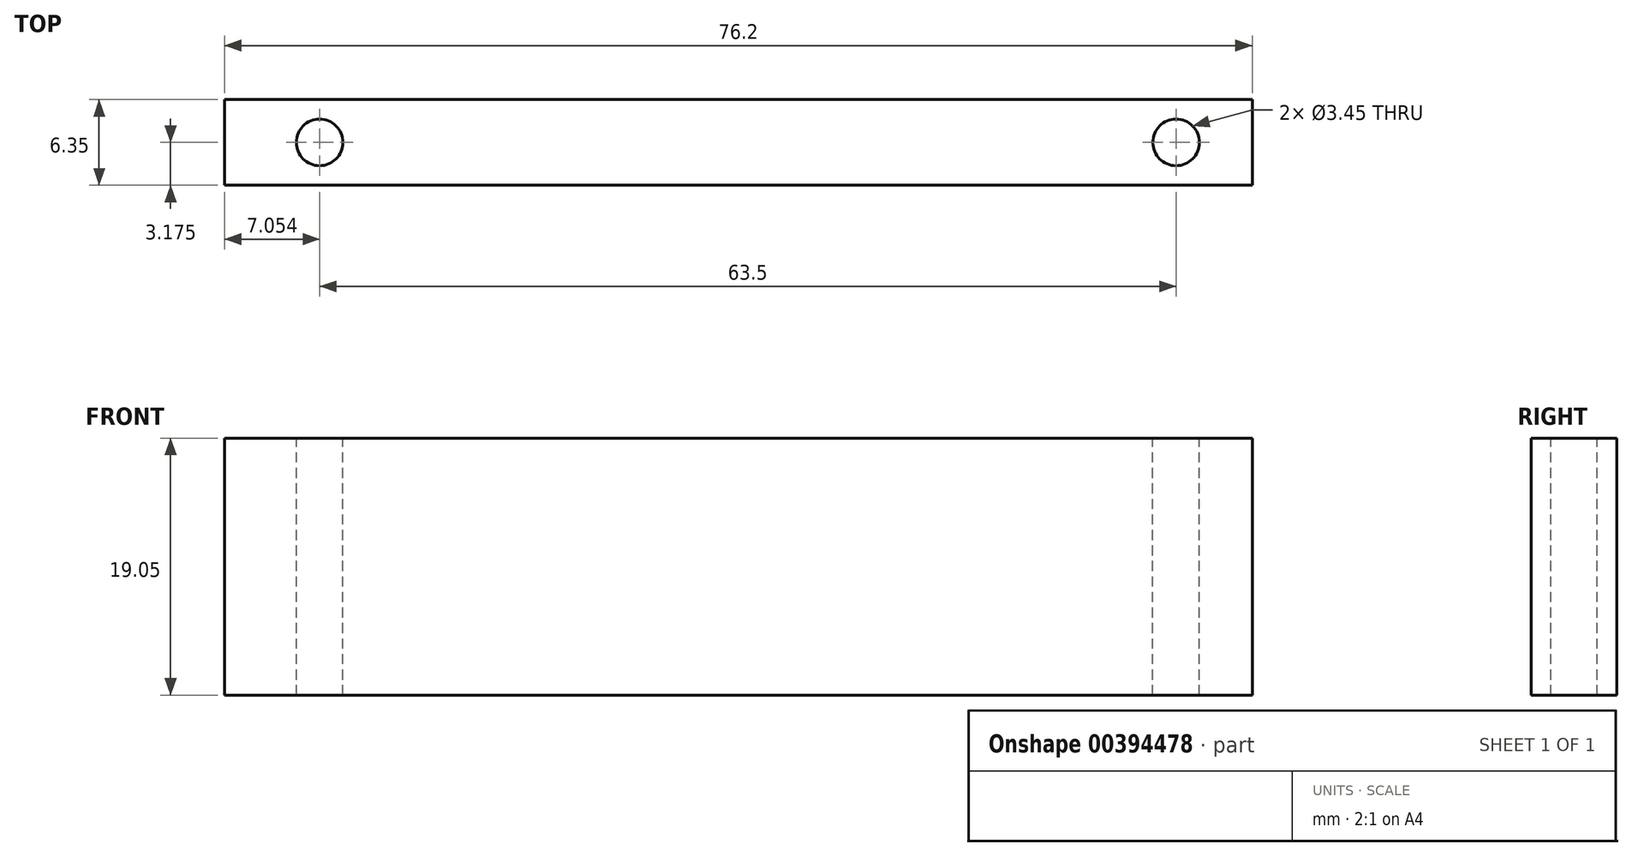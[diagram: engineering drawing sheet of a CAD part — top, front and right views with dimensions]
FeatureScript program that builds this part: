
annotation { "Feature Type Name" : "Feature", "Feature Type Description" : "" }
export const myFeature = defineFeature(function(context is Context, id is Id, definition is map)
    precondition{}
    {
        {
            var Q0;
            Q0=qCreatedBy(makeId("Top.planeOp"),FACE);
            var sketch = newSketch(context, id + "F0", { "sketchPlane" : qUnion([Q0])});
            skLineSegment(sketch, "E0.bottom", {"start": v(0, 0) * mm, "end": v(76.2, 0) * mm});
            skLineSegment(sketch, "E0.top", {"start": v(0, 6.35) * mm, "end": v(76.2, 6.35) * mm});
            skLineSegment(sketch, "E0.left", {"start": v(0, 0) * mm, "end": v(0, 6.35) * mm});
            skLineSegment(sketch, "E0.right", {"start": v(76.2, 0) * mm, "end": v(76.2, 6.35) * mm});
            skSolve(sketch);
        }
        {
            var Q0;
            Q0 = qSketchRegion(id + "F0", true);
            extrude(context, id + "F1", {"entities" : qUnion([Q0]), "depth" : 19.05 * mm});
        }
        {
            var Q0;
            Q0=makeQuery(id+"F1.opExtrude","CAP_FACE",FACE,{"disambiguationData":[OSD([sQuery(id+"F0.wireOp",EDGE,"E0.bottom"),sQuery(id+"F0.wireOp",EDGE,"E0.top"),sQuery(id+"F0.wireOp",EDGE,"E0.left"),sQuery(id+"F0.wireOp",EDGE,"E0.right")])],"isStart":false});
            var sketch = newSketch(context, id + "F2", { "sketchPlane" : qUnion([Q0])});
            skCircle(sketch, "E1", {"center": v(7.05, 3.17) * mm, "radius": 1.73 * mm});
            skCircle(sketch, "E2", {"center": v(70.55, 3.17) * mm, "radius": 1.73 * mm});
            skLineSegment(sketch, "E3", {"start": v(0, 3.18) * mm, "end": v(76.2, 3.18) * mm, "construction": true});
            skLineSegment(sketch, "E4", {"start": v(7.05, 3.17) * mm, "end": v(70.55, 3.17) * mm, "construction": true});
            skPoint(sketch, "E5", {"position": v(38.1, 3.17) * mm});
            skSolve(sketch);
        }
        {
            var Q0;
            Q0 = qSketchRegion(id + "F2", true);
            extrude(context, id + "F3", {"entities" : qUnion([Q0]), "operationType" : NewBodyOperationType.REMOVE, "endBound" : BoundingType.THROUGH_ALL, "oppositeDirection" : true, "depth" : 25.4 * mm});
        }
    });
